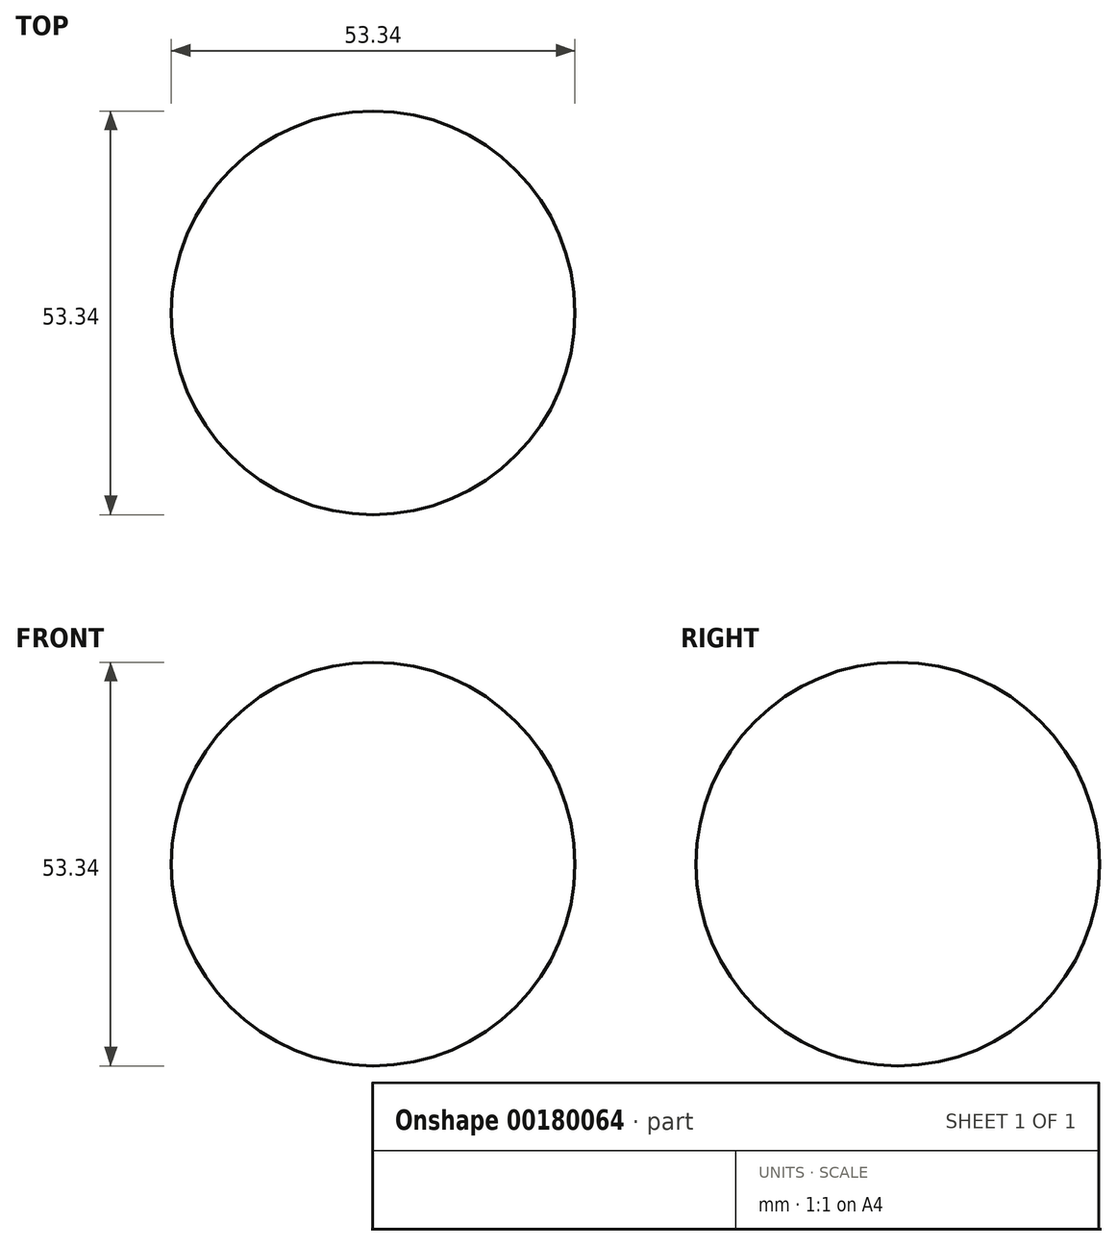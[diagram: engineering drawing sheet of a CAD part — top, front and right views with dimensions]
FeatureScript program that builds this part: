
annotation { "Feature Type Name" : "Feature", "Feature Type Description" : "" }
export const myFeature = defineFeature(function(context is Context, id is Id, definition is map)
    precondition{}
    {
        {
            var Q0;
            Q0=qCreatedBy(makeId("Front.planeOp"),FACE);
            var sketch = newSketch(context, id + "F0", { "sketchPlane" : qUnion([Q0])});
            skArc(sketch, "E0", {"start": v(0, 26.67) * mm, "mid": v(26.67, 0) * mm, "end": v(0, -26.67) * mm});
            skLineSegment(sketch, "E1", {"start": v(0, 26.67) * mm, "end": v(0, -26.67) * mm});
            skSolve(sketch);
        }
        {
            var Q0;
            Q0 = qSketchRegion(id + "F0", true);
            var Q1;
            Q1=sQuery(id+"F0.wireOp",EDGE,"E1");
            revolve(context, id + "F1", {"entities" : qUnion([Q0]), "axis" : qUnion([Q1]), "revolveType" : RevolveType.FULL});
        }
    });
